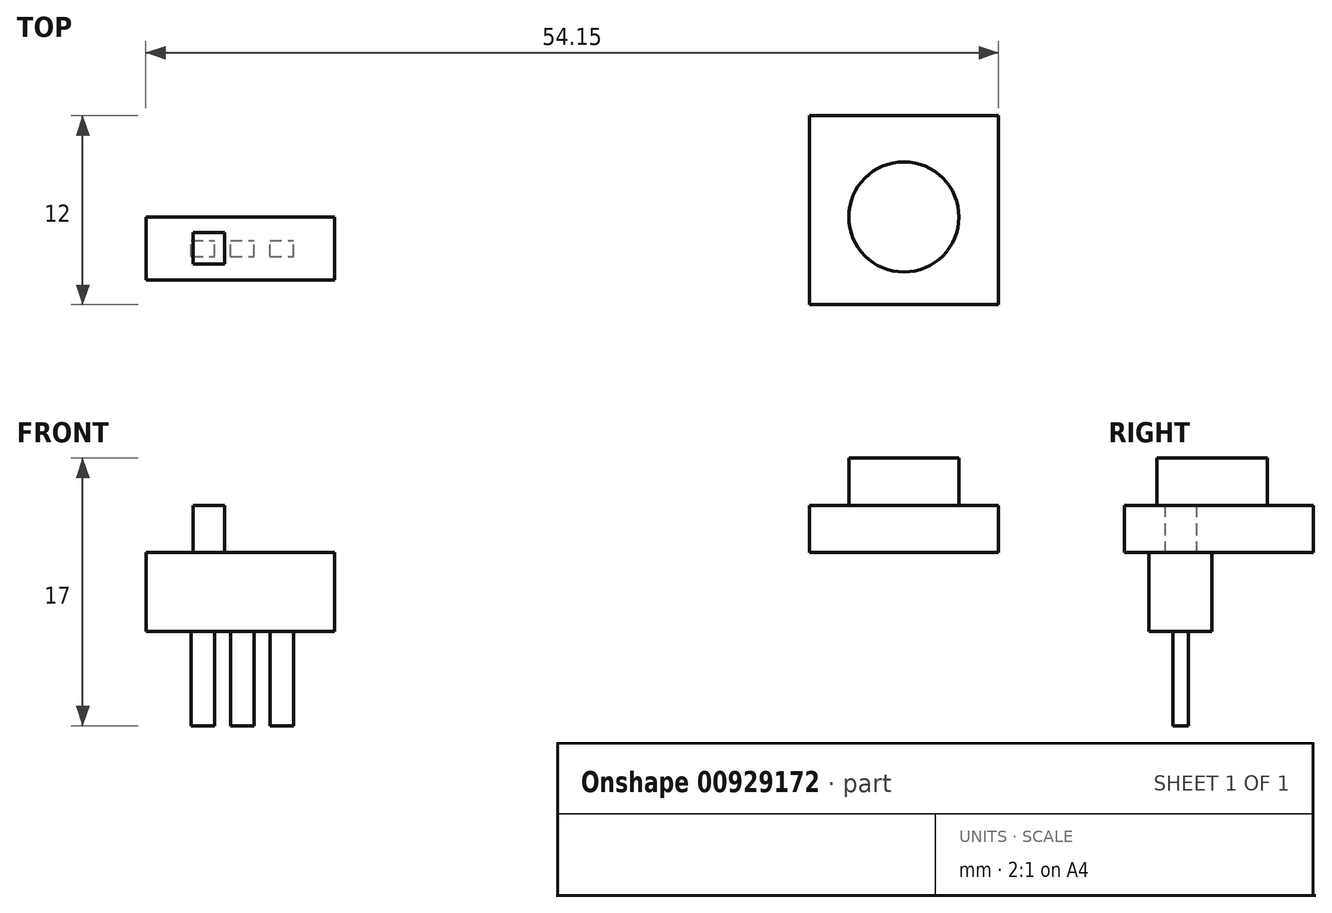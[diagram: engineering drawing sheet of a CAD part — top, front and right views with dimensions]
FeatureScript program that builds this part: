
annotation { "Feature Type Name" : "Feature", "Feature Type Description" : "" }
export const myFeature = defineFeature(function(context is Context, id is Id, definition is map)
    precondition{}
    {
        {
            var Q0;
            Q0=qCreatedBy(makeId("Front.planeOp"),FACE);
            var sketch = newSketch(context, id + "F0", { "sketchPlane" : qUnion([Q0])});
            skLineSegment(sketch, "E0.bottom", {"start": v(-1.85, -5) * mm, "end": v(-13.85, -5) * mm});
            skLineSegment(sketch, "E0.top", {"start": v(-1.85, 0) * mm, "end": v(-13.85, 0) * mm});
            skLineSegment(sketch, "E0.left", {"start": v(-1.85, -5) * mm, "end": v(-1.85, 0) * mm});
            skLineSegment(sketch, "E0.right", {"start": v(-13.85, -5) * mm, "end": v(-13.85, 0) * mm});
            skSolve(sketch);
        }
        {
            var Q0;
            Q0=makeQuery(id+"F0.imprint","IMPRINT",FACE,{"disambiguationData":[TD([[makeQuery(id+"F0.imprint","IMPRINT",EDGE,{"derivedFrom":sQuery(id+"F0.wireOp",EDGE,"E0.bottom")}),-1.0]])]});
            extrude(context, id + "F1", {"entities" : qUnion([Q0]), "depth" : 4 * mm, "offsetDistance" : 25 * mm});
        }
        {
            var Q0;
            Q0=makeQuery(id+"F1.opExtrude","SWEPT_FACE",FACE,{"disambiguationData":[OSD([sQuery(id+"F0.wireOp",EDGE,"E0.top")])]});
            var sketch = newSketch(context, id + "F2", { "sketchPlane" : qUnion([Q0])});
            skLineSegment(sketch, "E1.bottom", {"start": v(-10.85, -1) * mm, "end": v(-8.85, -1) * mm});
            skLineSegment(sketch, "E1.top", {"start": v(-10.85, -3) * mm, "end": v(-8.85, -3) * mm});
            skLineSegment(sketch, "E1.left", {"start": v(-10.85, -1) * mm, "end": v(-10.85, -3) * mm});
            skLineSegment(sketch, "E1.right", {"start": v(-8.85, -1) * mm, "end": v(-8.85, -3) * mm});
            skSolve(sketch);
        }
        {
            var Q0;
            Q0=makeQuery(id+"F2.imprint","IMPRINT",FACE,{"disambiguationData":[TD([[makeQuery(id+"F2.imprint","IMPRINT",EDGE,{"derivedFrom":sQuery(id+"F2.wireOp",EDGE,"E1.bottom")}),-1.0]])]});
            extrude(context, id + "F3", {"entities" : qUnion([Q0]), "operationType" : NewBodyOperationType.ADD, "depth" : 3 * mm, "offsetDistance" : 25 * mm});
        }
        {
            var Q0;
            Q0=makeQuery(id+"F1.opExtrude","SWEPT_FACE",FACE,{"disambiguationData":[OSD([sQuery(id+"F0.wireOp",EDGE,"E0.bottom")])]});
            var sketch = newSketch(context, id + "F4", { "sketchPlane" : qUnion([Q0])});
            skLineSegment(sketch, "E2.bottom", {"start": v(-10.97, 2.5) * mm, "end": v(-9.47, 2.5) * mm});
            skLineSegment(sketch, "E2.top", {"start": v(-10.97, 1.5) * mm, "end": v(-9.47, 1.5) * mm});
            skLineSegment(sketch, "E2.left", {"start": v(-10.97, 2.5) * mm, "end": v(-10.97, 1.5) * mm});
            skLineSegment(sketch, "E2.right", {"start": v(-9.47, 2.5) * mm, "end": v(-9.47, 1.5) * mm});
            skLineSegment(sketch, "E3.bottom", {"start": v(-8.47, 2.5) * mm, "end": v(-6.97, 2.5) * mm});
            skLineSegment(sketch, "E3.top", {"start": v(-8.47, 1.5) * mm, "end": v(-6.97, 1.5) * mm});
            skLineSegment(sketch, "E3.left", {"start": v(-8.47, 2.5) * mm, "end": v(-8.47, 1.5) * mm});
            skLineSegment(sketch, "E3.right", {"start": v(-6.97, 2.5) * mm, "end": v(-6.97, 1.5) * mm});
            skLineSegment(sketch, "E4.bottom", {"start": v(-5.97, 2.5) * mm, "end": v(-4.47, 2.5) * mm});
            skLineSegment(sketch, "E4.top", {"start": v(-5.97, 1.5) * mm, "end": v(-4.47, 1.5) * mm});
            skLineSegment(sketch, "E4.left", {"start": v(-5.97, 2.5) * mm, "end": v(-5.97, 1.5) * mm});
            skLineSegment(sketch, "E4.right", {"start": v(-4.47, 2.5) * mm, "end": v(-4.47, 1.5) * mm});
            skSolve(sketch);
        }
        {
            var Q0;
            Q0=makeQuery(id+"F4.imprint","IMPRINT",FACE,{"disambiguationData":[TD([[makeQuery(id+"F4.imprint","IMPRINT",EDGE,{"derivedFrom":sQuery(id+"F4.wireOp",EDGE,"E2.bottom")}),-1.0]])]});
            var Q1;
            Q1=makeQuery(id+"F4.imprint","IMPRINT",FACE,{"disambiguationData":[TD([[makeQuery(id+"F4.imprint","IMPRINT",EDGE,{"derivedFrom":sQuery(id+"F4.wireOp",EDGE,"E3.bottom")}),-1.0]])]});
            var Q2;
            Q2=makeQuery(id+"F4.imprint","IMPRINT",FACE,{"disambiguationData":[TD([[makeQuery(id+"F4.imprint","IMPRINT",EDGE,{"derivedFrom":sQuery(id+"F4.wireOp",EDGE,"E4.bottom")}),-1.0]])]});
            extrude(context, id + "F5", {"entities" : qUnion([Q0, Q1, Q2]), "operationType" : NewBodyOperationType.ADD, "depth" : 6 * mm, "offsetDistance" : 25 * mm});
        }
        {
            var Q0;
            Q0=qCreatedBy(makeId("Top.planeOp"),FACE);
            var sketch = newSketch(context, id + "F6", { "sketchPlane" : qUnion([Q0])});
            skLineSegment(sketch, "E5.bottom", {"start": v(40.3, 6.43) * mm, "end": v(28.3, 6.43) * mm});
            skLineSegment(sketch, "E5.top", {"start": v(40.3, -5.57) * mm, "end": v(28.3, -5.57) * mm});
            skLineSegment(sketch, "E5.left", {"start": v(40.3, 6.43) * mm, "end": v(40.3, -5.57) * mm});
            skLineSegment(sketch, "E5.right", {"start": v(28.3, 6.43) * mm, "end": v(28.3, -5.57) * mm});
            skSolve(sketch);
        }
        {
            var Q0;
            Q0 = qSketchRegion(id + "F6", true);
            extrude(context, id + "F7", {"entities" : qUnion([Q0]), "depth" : 3 * mm, "offsetDistance" : 25 * mm});
        }
        {
            var Q0;
            Q0=makeQuery(id+"F7.opExtrude","CAP_FACE",FACE,{"disambiguationData":[OSD([sQuery(id+"F6.wireOp",EDGE,"E5.bottom"),sQuery(id+"F6.wireOp",EDGE,"E5.top"),sQuery(id+"F6.wireOp",EDGE,"E5.left"),sQuery(id+"F6.wireOp",EDGE,"E5.right")])],"isStart":false});
            var sketch = newSketch(context, id + "F8", { "sketchPlane" : qUnion([Q0])});
            skCircle(sketch, "E6", {"center": v(34.3, 0) * mm, "radius": 3.5 * mm});
            skPoint(sketch, "E6.centerSnap0", {"position": v(34.3, 6.43) * mm});
            skSolve(sketch);
        }
        {
            var Q0;
            Q0 = qSketchRegion(id + "F8", true);
            extrude(context, id + "F9", {"entities" : qUnion([Q0]), "operationType" : NewBodyOperationType.ADD, "depth" : 3 * mm, "offsetDistance" : 25 * mm});
        }
    });
